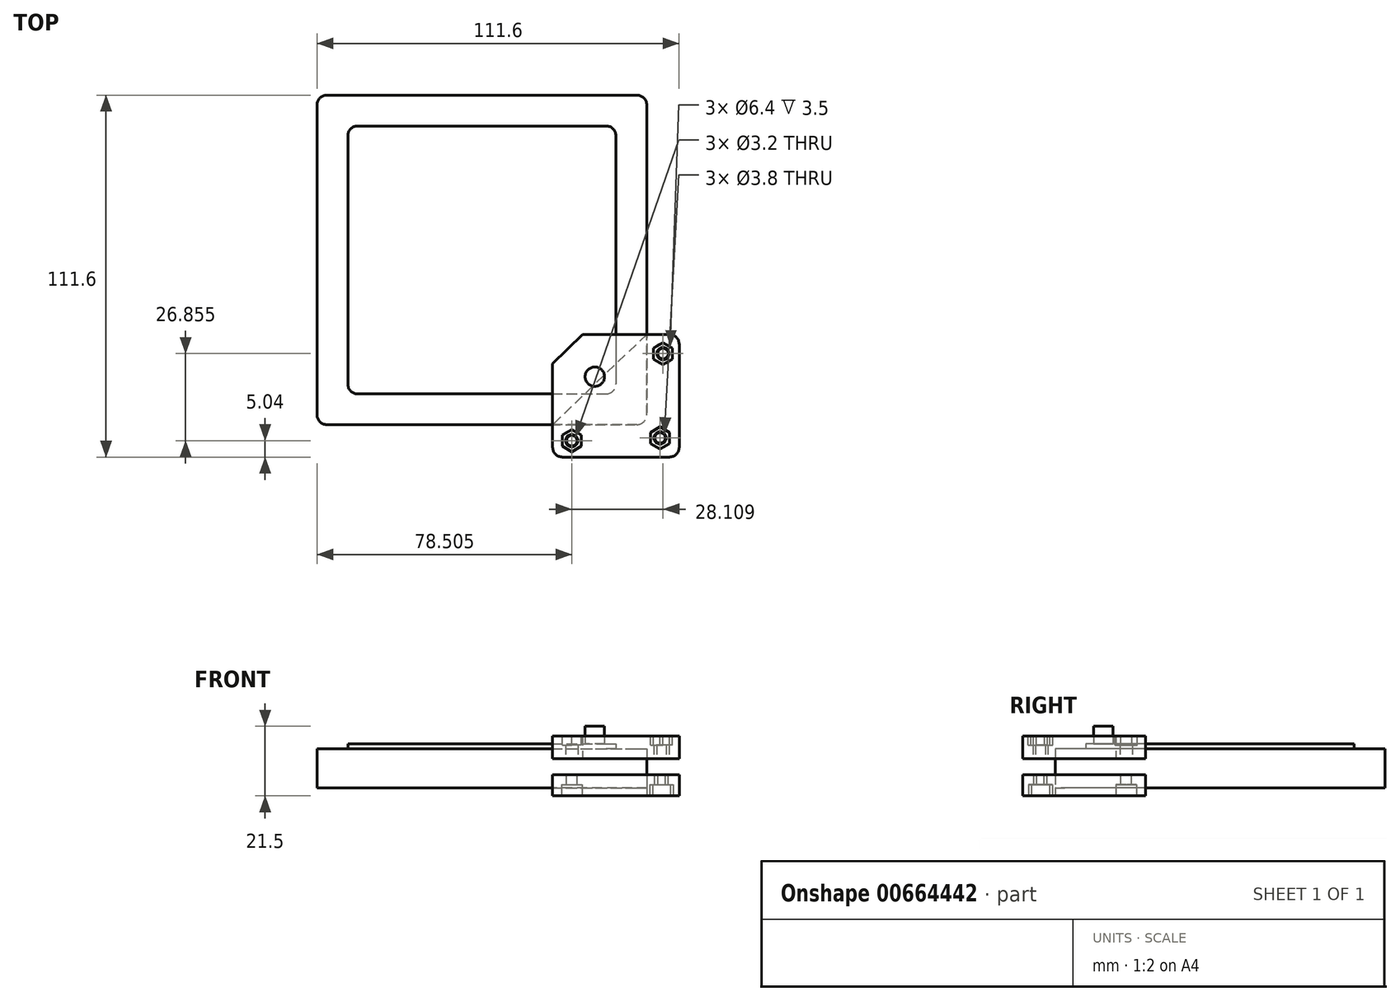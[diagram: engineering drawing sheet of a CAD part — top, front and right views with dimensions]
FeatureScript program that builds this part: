
annotation { "Feature Type Name" : "Feature", "Feature Type Description" : "" }
export const myFeature = defineFeature(function(context is Context, id is Id, definition is map)
    precondition{}
    {
        {
            var Q0;
            Q0=qCreatedBy(makeId("Top.planeOp"),FACE);
            var sketch = newSketch(context, id + "F0", { "sketchPlane" : qUnion([Q0])});
            skLineSegment(sketch, "E0.bottom", {"start": v(-94.5, 32.37) * mm, "end": v(1.1, 32.37) * mm});
            skLineSegment(sketch, "E0.top", {"start": v(-94.5, -69.23) * mm, "end": v(1.1, -69.23) * mm});
            skLineSegment(sketch, "E0.left", {"start": v(-97.5, 29.37) * mm, "end": v(-97.5, -66.23) * mm});
            skLineSegment(sketch, "E0.right", {"start": v(4.1, 29.37) * mm, "end": v(4.1, -66.23) * mm});
            skPoint(sketch, "E1.visualSharp", {"position": v(-97.5, 32.37) * mm});
            skArc(sketch, "E1.filletArc", {"start": v(-94.5, 32.37) * mm, "mid": v(-96.62, 31.49) * mm, "end": v(-97.5, 29.37) * mm});
            skPoint(sketch, "E2.visualSharp", {"position": v(-97.5, -69.23) * mm});
            skArc(sketch, "E2.filletArc", {"start": v(-97.5, -66.23) * mm, "mid": v(-96.62, -68.36) * mm, "end": v(-94.5, -69.23) * mm});
            skPoint(sketch, "E3.visualSharp", {"position": v(4.1, -69.23) * mm});
            skArc(sketch, "E3.filletArc", {"start": v(1.1, -69.23) * mm, "mid": v(3.23, -68.36) * mm, "end": v(4.1, -66.23) * mm});
            skPoint(sketch, "E4.visualSharp", {"position": v(4.1, 32.37) * mm});
            skArc(sketch, "E4.filletArc", {"start": v(4.1, 29.37) * mm, "mid": v(3.23, 31.49) * mm, "end": v(1.1, 32.37) * mm});
            skLineSegment(sketch, "E5.0", {"start": v(-85, 22.87) * mm, "end": v(-8.4, 22.87) * mm});
            skLineSegment(sketch, "E5.1", {"start": v(-88, 19.87) * mm, "end": v(-88, -56.73) * mm});
            skLineSegment(sketch, "E5.2", {"start": v(-85, -59.73) * mm, "end": v(-8.4, -59.73) * mm});
            skLineSegment(sketch, "E5.3", {"start": v(-5.4, 19.87) * mm, "end": v(-5.4, -56.73) * mm});
            skPoint(sketch, "E6.visualSharp", {"position": v(-88, 22.87) * mm});
            skArc(sketch, "E6.filletArc", {"start": v(-85, 22.87) * mm, "mid": v(-87.12, 21.99) * mm, "end": v(-88, 19.87) * mm});
            skPoint(sketch, "E7.visualSharp", {"position": v(-88, -59.73) * mm});
            skArc(sketch, "E7.filletArc", {"start": v(-88, -56.73) * mm, "mid": v(-87.12, -58.86) * mm, "end": v(-85, -59.73) * mm});
            skPoint(sketch, "E8.visualSharp", {"position": v(-5.4, -59.73) * mm});
            skArc(sketch, "E8.filletArc", {"start": v(-8.4, -59.73) * mm, "mid": v(-6.27, -58.86) * mm, "end": v(-5.4, -56.73) * mm});
            skPoint(sketch, "E9.visualSharp", {"position": v(-5.4, 22.87) * mm});
            skArc(sketch, "E9.filletArc", {"start": v(-5.4, 19.87) * mm, "mid": v(-6.27, 21.99) * mm, "end": v(-8.4, 22.87) * mm});
            skCircle(sketch, "E10", {"center": v(-11.9, -54.43) * mm, "radius": 3 * mm});
            skSolve(sketch);
        }
        {
            var Q0;
            Q0=makeQuery(id+"F0.imprint","IMPRINT",FACE,{"disambiguationData":[TD([[makeQuery(id+"F0.imprint","IMPRINT",EDGE,{"derivedFrom":sQuery(id+"F0.wireOp",EDGE,"E0.bottom")}),-1.0]])]});
            extrude(context, id + "F1", {"entities" : qUnion([Q0]), "depth" : 12 * mm, "offsetDistance" : 25 * mm});
        }
        {
            var Q0;
            Q0=makeQuery(id+"F0.imprint","IMPRINT",FACE,{"disambiguationData":[TD([[makeQuery(id+"F0.imprint","IMPRINT",EDGE,{"derivedFrom":sQuery(id+"F0.wireOp",EDGE,"E5.0")}),-1.0]])]});
            extrude(context, id + "F2", {"entities" : qUnion([Q0]), "operationType" : NewBodyOperationType.ADD, "depth" : 13.5 * mm, "offsetDistance" : 25 * mm});
        }
        {
            var Q0;
            Q0=makeQuery(id+"F0.imprint","IMPRINT",FACE,{"disambiguationData":[TD([[makeQuery(id+"F0.imprint","IMPRINT",EDGE,{"derivedFrom":sQuery(id+"F0.wireOp",EDGE,"E10")}),1.0]])]});
            extrude(context, id + "F3", {"entities" : qUnion([Q0]), "operationType" : NewBodyOperationType.ADD, "depth" : 19 * mm, "offsetDistance" : 25 * mm});
        }
        {
            var Q0;
            Q0=qCreatedBy(makeId("Top.planeOp"),FACE);
            var sketch = newSketch(context, id + "F4", { "sketchPlane" : qUnion([Q0])});
            skLineSegment(sketch, "E11.bottom", {"start": v(11.1, -41.43) * mm, "end": v(-15.72, -41.43) * mm});
            skLineSegment(sketch, "E11.top", {"start": v(11.1, -79.23) * mm, "end": v(-21.9, -79.23) * mm});
            skLineSegment(sketch, "E11.left", {"start": v(14.1, -44.43) * mm, "end": v(14.1, -76.23) * mm});
            skLineSegment(sketch, "E11.right", {"start": v(-24.9, -50.5) * mm, "end": v(-24.9, -76.23) * mm});
            skArc(sketch, "E12.filletArc", {"start": v(-24.9, -76.23) * mm, "mid": v(-24.02, -78.36) * mm, "end": v(-21.9, -79.23) * mm});
            skPoint(sketch, "E13.visualSharp", {"position": v(14.1, -79.23) * mm});
            skArc(sketch, "E13.filletArc", {"start": v(11.1, -79.23) * mm, "mid": v(13.23, -78.36) * mm, "end": v(14.1, -76.23) * mm});
            skPoint(sketch, "E14.visualSharp", {"position": v(14.1, -41.43) * mm});
            skArc(sketch, "E14.filletArc", {"start": v(14.1, -44.43) * mm, "mid": v(13.23, -42.31) * mm, "end": v(11.1, -41.43) * mm});
            skCircle(sketch, "E15", {"center": v(9.11, -47.33) * mm, "radius": 1.9 * mm});
            skCircle(sketch, "E16", {"center": v(-19, -74.19) * mm, "radius": 1.9 * mm});
            skCircle(sketch, "E17", {"center": v(8.2, -73.33) * mm, "radius": 1.9 * mm});
            skPoint(sketch, "E18", {"position": v(-15.72, -41.43) * mm});
            skPoint(sketch, "E19", {"position": v(-24.9, -50.5) * mm});
            skLineSegment(sketch, "E20", {"start": v(-15.72, -41.43) * mm, "end": v(-24.9, -50.5) * mm});
            skPoint(sketch, "E21", {"position": v(4.12, -41.43) * mm});
            skPoint(sketch, "E22", {"position": v(4.12, -79.23) * mm});
            skLineSegment(sketch, "E23", {"start": v(4.12, -41.43) * mm, "end": v(4.12, -79.23) * mm, "construction": true});
            skPoint(sketch, "E24", {"position": v(14.1, -47.33) * mm});
            skPoint(sketch, "E25", {"position": v(4.12, -47.33) * mm});
            skLineSegment(sketch, "E26", {"start": v(14.1, -47.33) * mm, "end": v(4.12, -47.33) * mm, "construction": true});
            skPoint(sketch, "E27", {"position": v(-19, -69.14) * mm});
            skPoint(sketch, "E28", {"position": v(-19, -79.23) * mm});
            skLineSegment(sketch, "E29", {"start": v(-19, -69.14) * mm, "end": v(-19, -79.23) * mm, "construction": true});
            skLineSegment(sketch, "E30", {"start": v(-24.9, -69.14) * mm, "end": v(14.1, -69.14) * mm, "construction": true});
            skSolve(sketch);
        }
        {
            var Q0;
            Q0 = qSketchRegion(id + "F4", true);
            extrude(context, id + "F5", {"entities" : qUnion([Q0]), "depth" : 7 * mm, "offsetDistance" : 25 * mm});
        }
        {
            var Q0;
            Q0=makeQuery(id+"F5.opExtrude","SWEPT_BODY",BODY,{"disambiguationData":[OSD([sQuery(id+"F4.wireOp",EDGE,"E11.bottom"),sQuery(id+"F4.wireOp",EDGE,"E11.top"),sQuery(id+"F4.wireOp",EDGE,"E11.left"),sQuery(id+"F4.wireOp",EDGE,"E11.right")])]});
            transform(context, id + "F6", {"entities" : qUnion([Q0]), "transformType" : TransformType.TRANSLATION_3D, "dx" : 0 * mm, "dy" : 0 * mm, "dz" : 3 * mm, "makeCopy" : false});
        }
        {
            var Q0;
            Q0=qCreatedBy(makeId("Top.planeOp"),FACE);
            var sketch = newSketch(context, id + "F7", { "sketchPlane" : qUnion([Q0])});
            skLineSegment(sketch, "E31", {"start": v(4.1, -41.43) * mm, "end": v(-24.9, -69.23) * mm});
            skLineSegment(sketch, "E32", {"start": v(-24.9, -69.23) * mm, "end": v(-24.9, -76.23) * mm});
            skLineSegment(sketch, "E33", {"start": v(-21.9, -79.23) * mm, "end": v(11.1, -79.23) * mm});
            skLineSegment(sketch, "E34", {"start": v(14.1, -76.23) * mm, "end": v(14.1, -44.43) * mm});
            skLineSegment(sketch, "E35", {"start": v(11.1, -41.43) * mm, "end": v(4.1, -41.43) * mm});
            skPoint(sketch, "E36.visualSharp", {"position": v(14.1, -41.43) * mm});
            skArc(sketch, "E36.filletArc", {"start": v(14.1, -44.43) * mm, "mid": v(13.23, -42.31) * mm, "end": v(11.1, -41.43) * mm});
            skPoint(sketch, "E37.visualSharp", {"position": v(14.1, -79.23) * mm});
            skArc(sketch, "E37.filletArc", {"start": v(11.1, -79.23) * mm, "mid": v(13.23, -78.36) * mm, "end": v(14.1, -76.23) * mm});
            skPoint(sketch, "E38.visualSharp", {"position": v(-25.8, -79.23) * mm});
            skArc(sketch, "E38.filletArc", {"start": v(-24.9, -76.23) * mm, "mid": v(-24.02, -78.36) * mm, "end": v(-21.9, -79.23) * mm});
            skSolve(sketch);
        }
        {
            var Q0;
            Q0=makeQuery(id+"F5.opExtrude","CAP_FACE",FACE,{"disambiguationData":[OSD([sQuery(id+"F4.wireOp",EDGE,"E11.bottom"),sQuery(id+"F4.wireOp",EDGE,"E11.top"),sQuery(id+"F4.wireOp",EDGE,"E11.left"),sQuery(id+"F4.wireOp",EDGE,"E11.right"),sQuery(id+"F4.wireOp",EDGE,"E12.filletArc"),sQuery(id+"F4.wireOp",EDGE,"E13.filletArc"),sQuery(id+"F4.wireOp",EDGE,"E14.filletArc"),sQuery(id+"F4.wireOp",EDGE,"E15"),sQuery(id+"F4.wireOp",EDGE,"E16"),sQuery(id+"F4.wireOp",EDGE,"E17")])],"isStart":false});
            cPlane(context, id + "F8", {"entities" : qUnion([Q0]), "cplaneType" : CPlaneType.OFFSET, "offset" : 0 * mm, "width" : 150 * mm, "height" : 150 * mm});
        }
        {
            var Q0;
            Q0=qCreatedBy(id+"F8.planeOp",FACE);
            var sketch = newSketch(context, id + "F9", { "sketchPlane" : qUnion([Q0])});
            skCircle(sketch, "E39.cCircle", {"center": v(8.2, -73.33) * mm, "radius": 3.4 * mm, "construction": true});
            skLineSegment(sketch, "E39.0", {"start": v(5.25, -71.63) * mm, "end": v(8.2, -69.93) * mm});
            skLineSegment(sketch, "E39.1", {"start": v(8.2, -69.93) * mm, "end": v(11.15, -71.63) * mm});
            skLineSegment(sketch, "E39.2", {"start": v(11.15, -71.63) * mm, "end": v(11.15, -75.04) * mm});
            skLineSegment(sketch, "E39.3", {"start": v(11.15, -75.04) * mm, "end": v(8.2, -76.74) * mm});
            skLineSegment(sketch, "E39.4", {"start": v(8.2, -76.74) * mm, "end": v(5.25, -75.04) * mm});
            skLineSegment(sketch, "E39.5", {"start": v(5.25, -75.04) * mm, "end": v(5.25, -71.63) * mm});
            skCircle(sketch, "E40.cCircle", {"center": v(9.11, -47.33) * mm, "radius": 3.4 * mm, "construction": true});
            skLineSegment(sketch, "E40.0", {"start": v(6.16, -45.63) * mm, "end": v(9.11, -43.93) * mm});
            skLineSegment(sketch, "E40.1", {"start": v(9.11, -43.93) * mm, "end": v(12.06, -45.63) * mm});
            skLineSegment(sketch, "E40.2", {"start": v(12.06, -45.63) * mm, "end": v(12.06, -49.04) * mm});
            skLineSegment(sketch, "E40.3", {"start": v(12.06, -49.04) * mm, "end": v(9.11, -50.74) * mm});
            skLineSegment(sketch, "E40.4", {"start": v(9.11, -50.74) * mm, "end": v(6.16, -49.04) * mm});
            skLineSegment(sketch, "E40.5", {"start": v(6.16, -49.04) * mm, "end": v(6.16, -45.63) * mm});
            skCircle(sketch, "E41.cCircle", {"center": v(-19, -74.19) * mm, "radius": 3.4 * mm, "construction": true});
            skLineSegment(sketch, "E41.0", {"start": v(-21.95, -72.49) * mm, "end": v(-19, -70.78) * mm});
            skLineSegment(sketch, "E41.1", {"start": v(-19, -70.78) * mm, "end": v(-16.05, -72.49) * mm});
            skLineSegment(sketch, "E41.2", {"start": v(-16.05, -72.49) * mm, "end": v(-16.05, -75.9) * mm});
            skLineSegment(sketch, "E41.3", {"start": v(-16.05, -75.9) * mm, "end": v(-19, -77.6) * mm});
            skLineSegment(sketch, "E41.4", {"start": v(-19, -77.6) * mm, "end": v(-21.95, -75.9) * mm});
            skLineSegment(sketch, "E41.5", {"start": v(-21.95, -75.9) * mm, "end": v(-21.95, -72.49) * mm});
            skSolve(sketch);
        }
        {
            var Q0;
            Q0=makeQuery(id+"F9.imprint","IMPRINT",FACE,{"disambiguationData":[TD([[makeQuery(id+"F9.imprint","IMPRINT",EDGE,{"derivedFrom":sQuery(id+"F9.wireOp",EDGE,"E39.0")}),-1.0]])]});
            var Q1;
            Q1=makeQuery(id+"F9.imprint","IMPRINT",FACE,{"disambiguationData":[TD([[makeQuery(id+"F9.imprint","IMPRINT",EDGE,{"derivedFrom":sQuery(id+"F9.wireOp",EDGE,"E40.0")}),-1.0]])]});
            var Q2;
            Q2=makeQuery(id+"F9.imprint","IMPRINT",FACE,{"disambiguationData":[TD([[makeQuery(id+"F9.imprint","IMPRINT",EDGE,{"derivedFrom":sQuery(id+"F9.wireOp",EDGE,"E41.0")}),-1.0]])]});
            extrude(context, id + "F10", {"entities" : qUnion([Q0, Q1, Q2]), "operationType" : NewBodyOperationType.REMOVE, "oppositeDirection" : true, "depth" : 2.8 * mm, "offsetDistance" : 25 * mm});
        }
        {
            var Q0;
            Q0=makeQuery(id+"F5.opExtrude","SWEPT_BODY",BODY,{"disambiguationData":[OSD([sQuery(id+"F4.wireOp",EDGE,"E11.bottom"),sQuery(id+"F4.wireOp",EDGE,"E11.top"),sQuery(id+"F4.wireOp",EDGE,"E11.left"),sQuery(id+"F4.wireOp",EDGE,"E11.right"),sQuery(id+"F4.wireOp",EDGE,"E12.filletArc"),sQuery(id+"F4.wireOp",EDGE,"E13.filletArc"),sQuery(id+"F4.wireOp",EDGE,"E14.filletArc"),sQuery(id+"F4.wireOp",EDGE,"E15"),sQuery(id+"F4.wireOp",EDGE,"E16"),sQuery(id+"F4.wireOp",EDGE,"E17")])]});
            transform(context, id + "F11", {"entities" : qUnion([Q0]), "transformType" : TransformType.TRANSLATION_3D, "dx" : 0 * mm, "dy" : 0 * mm, "dz" : 8.8 * mm, "makeCopy" : false});
        }
        {
            var Q0;
            Q0=makeQuery(id+"F5.opExtrude","SWEPT_BODY",BODY,{"disambiguationData":[OSD([sQuery(id+"F4.wireOp",EDGE,"E11.bottom"),sQuery(id+"F4.wireOp",EDGE,"E11.top"),sQuery(id+"F4.wireOp",EDGE,"E11.left"),sQuery(id+"F4.wireOp",EDGE,"E11.right"),sQuery(id+"F4.wireOp",EDGE,"E12.filletArc"),sQuery(id+"F4.wireOp",EDGE,"E13.filletArc"),sQuery(id+"F4.wireOp",EDGE,"E14.filletArc"),sQuery(id+"F4.wireOp",EDGE,"E15"),sQuery(id+"F4.wireOp",EDGE,"E16"),sQuery(id+"F4.wireOp",EDGE,"E17")])]});
            transform(context, id + "F12", {"entities" : qUnion([Q0]), "transformType" : TransformType.TRANSLATION_3D, "dx" : 0 * mm, "dy" : 0 * mm, "dz" : -0.8 * mm, "makeCopy" : false});
        }
        {
            var Q0;
            Q0 = qSketchRegion(id + "F7", true);
            extrude(context, id + "F13", {"entities" : qUnion([Q0]), "depth" : 6.5 * mm, "offsetDistance" : 25 * mm});
        }
        {
            var Q0;
            Q0=makeQuery(id+"F13.opExtrude","SWEPT_BODY",BODY,{"disambiguationData":[OSD([sQuery(id+"F7.wireOp",EDGE,"E31"),sQuery(id+"F7.wireOp",EDGE,"E32"),sQuery(id+"F7.wireOp",EDGE,"E33"),sQuery(id+"F7.wireOp",EDGE,"E34"),sQuery(id+"F7.wireOp",EDGE,"E35"),sQuery(id+"F7.wireOp",EDGE,"E36.filletArc"),sQuery(id+"F7.wireOp",EDGE,"E37.filletArc"),sQuery(id+"F7.wireOp",EDGE,"E38.filletArc")])]});
            transform(context, id + "F14", {"entities" : qUnion([Q0]), "transformType" : TransformType.TRANSLATION_3D, "dx" : 0 * mm, "dy" : 0 * mm, "dz" : -2.5 * mm, "makeCopy" : false});
        }
        {
            var Q0;
            Q0=makeQuery(id+"F13.opExtrude","CAP_FACE",FACE,{"disambiguationData":[OSD([sQuery(id+"F7.wireOp",EDGE,"E31"),sQuery(id+"F7.wireOp",EDGE,"E32"),sQuery(id+"F7.wireOp",EDGE,"E33"),sQuery(id+"F7.wireOp",EDGE,"E34"),sQuery(id+"F7.wireOp",EDGE,"E35"),sQuery(id+"F7.wireOp",EDGE,"E36.filletArc"),sQuery(id+"F7.wireOp",EDGE,"E37.filletArc"),sQuery(id+"F7.wireOp",EDGE,"E38.filletArc")])],"isStart":true});
            cPlane(context, id + "F15", {"entities" : qUnion([Q0]), "cplaneType" : CPlaneType.OFFSET, "offset" : 0 * mm, "width" : 150 * mm, "height" : 150 * mm});
        }
        {
            var Q0;
            Q0=qCreatedBy(id+"F15.planeOp",FACE);
            var sketch = newSketch(context, id + "F16", { "sketchPlane" : qUnion([Q0])});
            skCircle(sketch, "E42", {"center": v(-19, 74.19) * mm, "radius": 3.2 * mm});
            skCircle(sketch, "E43", {"center": v(8.2, 73.33) * mm, "radius": 3.2 * mm});
            skCircle(sketch, "E44", {"center": v(9.11, 47.33) * mm, "radius": 3.2 * mm});
            skSolve(sketch);
        }
        {
            var Q0;
            Q0 = qSketchRegion(id + "F16", true);
            extrude(context, id + "F17", {"entities" : qUnion([Q0]), "operationType" : NewBodyOperationType.REMOVE, "oppositeDirection" : true, "depth" : 3.5 * mm, "offsetDistance" : 25 * mm});
        }
        {
            var Q0;
            Q0=makeQuery(id+"F13.opExtrude","CAP_FACE",FACE,{"disambiguationData":[OSD([sQuery(id+"F7.wireOp",EDGE,"E31"),sQuery(id+"F7.wireOp",EDGE,"E32"),sQuery(id+"F7.wireOp",EDGE,"E33"),sQuery(id+"F7.wireOp",EDGE,"E34"),sQuery(id+"F7.wireOp",EDGE,"E35"),sQuery(id+"F7.wireOp",EDGE,"E36.filletArc"),sQuery(id+"F7.wireOp",EDGE,"E37.filletArc"),sQuery(id+"F7.wireOp",EDGE,"E38.filletArc")])],"isStart":false});
            cPlane(context, id + "F18", {"entities" : qUnion([Q0]), "cplaneType" : CPlaneType.OFFSET, "offset" : 0 * mm, "width" : 150 * mm, "height" : 150 * mm});
        }
        {
            var Q0;
            Q0=qCreatedBy(id+"F18.planeOp",FACE);
            var sketch = newSketch(context, id + "F19", { "sketchPlane" : qUnion([Q0])});
            skCircle(sketch, "E45", {"center": v(-19, -74.19) * mm, "radius": 1.6 * mm});
            skCircle(sketch, "E46", {"center": v(9.11, -47.33) * mm, "radius": 1.6 * mm});
            skCircle(sketch, "E47", {"center": v(8.2, -73.33) * mm, "radius": 1.6 * mm});
            skSolve(sketch);
        }
        {
            var Q0;
            Q0 = qSketchRegion(id + "F19", true);
            extrude(context, id + "F20", {"entities" : qUnion([Q0]), "operationType" : NewBodyOperationType.REMOVE, "endBound" : BoundingType.THROUGH_ALL, "oppositeDirection" : true, "depth" : 25 * mm, "offsetDistance" : 25 * mm});
        }
        {
            var Q0;
            Q0=makeQuery(id+"F1.opExtrude","SWEPT_BODY",BODY,{"disambiguationData":[OSD([sQuery(id+"F0.wireOp",EDGE,"E0.bottom"),sQuery(id+"F0.wireOp",EDGE,"E0.top"),sQuery(id+"F0.wireOp",EDGE,"E0.left"),sQuery(id+"F0.wireOp",EDGE,"E0.right"),sQuery(id+"F0.wireOp",EDGE,"E1.filletArc"),sQuery(id+"F0.wireOp",EDGE,"E2.filletArc"),sQuery(id+"F0.wireOp",EDGE,"E3.filletArc"),sQuery(id+"F0.wireOp",EDGE,"E4.filletArc"),sQuery(id+"F0.wireOp",EDGE,"E5.0"),sQuery(id+"F0.wireOp",EDGE,"E5.1"),sQuery(id+"F0.wireOp",EDGE,"E5.2"),sQuery(id+"F0.wireOp",EDGE,"E5.3"),sQuery(id+"F0.wireOp",EDGE,"E6.filletArc"),sQuery(id+"F0.wireOp",EDGE,"E7.filletArc"),sQuery(id+"F0.wireOp",EDGE,"E8.filletArc"),sQuery(id+"F0.wireOp",EDGE,"E9.filletArc")])]});
            var Q1;
            Q1=makeQuery(id+"F13.opExtrude","SWEPT_BODY",BODY,{"disambiguationData":[OSD([sQuery(id+"F7.wireOp",EDGE,"E31"),sQuery(id+"F7.wireOp",EDGE,"E32"),sQuery(id+"F7.wireOp",EDGE,"E33"),sQuery(id+"F7.wireOp",EDGE,"E34"),sQuery(id+"F7.wireOp",EDGE,"E35"),sQuery(id+"F7.wireOp",EDGE,"E36.filletArc"),sQuery(id+"F7.wireOp",EDGE,"E37.filletArc"),sQuery(id+"F7.wireOp",EDGE,"E38.filletArc")])]});
            booleanBodies(context, id + "F21", {"operationType" : BooleanOperationType.SUBTRACTION, "tools" : qUnion([Q0]), "targets" : qUnion([Q1]), "keepTools" : true});
        }
        {
            var Q0;
            Q0=makeQuery(id+"F5.opExtrude","SWEPT_BODY",BODY,{"disambiguationData":[OSD([sQuery(id+"F4.wireOp",EDGE,"E11.bottom"),sQuery(id+"F4.wireOp",EDGE,"E11.top"),sQuery(id+"F4.wireOp",EDGE,"E11.left"),sQuery(id+"F4.wireOp",EDGE,"E11.right"),sQuery(id+"F4.wireOp",EDGE,"E12.filletArc"),sQuery(id+"F4.wireOp",EDGE,"E13.filletArc"),sQuery(id+"F4.wireOp",EDGE,"E14.filletArc"),sQuery(id+"F4.wireOp",EDGE,"E15"),sQuery(id+"F4.wireOp",EDGE,"E16"),sQuery(id+"F4.wireOp",EDGE,"E17"),sQuery(id+"F4.wireOp",EDGE,"E20")])]});
            transform(context, id + "F22", {"entities" : qUnion([Q0]), "transformType" : TransformType.TRANSLATION_3D, "dx" : 0 * mm, "dy" : 0 * mm, "dz" : -2 * mm, "makeCopy" : false});
        }
    });
